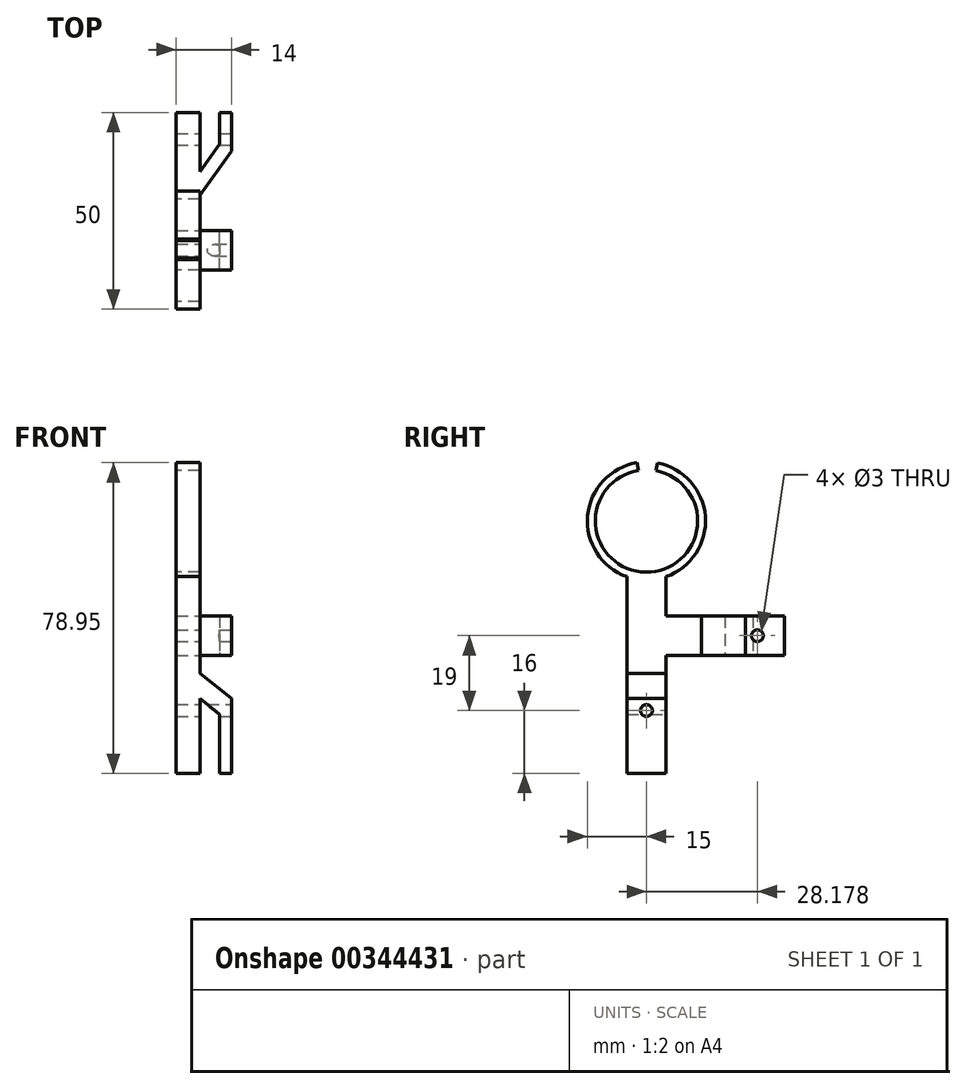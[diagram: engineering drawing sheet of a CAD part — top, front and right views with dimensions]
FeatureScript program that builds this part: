
annotation { "Feature Type Name" : "Feature", "Feature Type Description" : "" }
export const myFeature = defineFeature(function(context is Context, id is Id, definition is map)
    precondition{}
    {
        {
            var Q0;
            Q0=qCreatedBy(makeId("Front.planeOp"),FACE);
            var sketch = newSketch(context, id + "F0", { "sketchPlane" : qUnion([Q0])});
            skLineSegment(sketch, "E0", {"start": v(0, 0) * mm, "end": v(0, 50) * mm});
            skLineSegment(sketch, "E1", {"start": v(6, 50) * mm, "end": v(6, 25.4) * mm});
            skLineSegment(sketch, "E2", {"start": v(6, 25.4) * mm, "end": v(14, 19) * mm});
            skLineSegment(sketch, "E3", {"start": v(14, 19) * mm, "end": v(14, 0) * mm});
            skLineSegment(sketch, "E4", {"start": v(14, 0) * mm, "end": v(11, 0) * mm});
            skLineSegment(sketch, "E5", {"start": v(11, 0) * mm, "end": v(11, 15) * mm});
            skLineSegment(sketch, "E6", {"start": v(11, 15) * mm, "end": v(6, 19) * mm});
            skLineSegment(sketch, "E7", {"start": v(6, 19) * mm, "end": v(6, 0) * mm});
            skLineSegment(sketch, "E8", {"start": v(6, 0) * mm, "end": v(0, 0) * mm});
            skLineSegment(sketch, "E9", {"start": v(6, 50) * mm, "end": v(0, 50) * mm});
            skSolve(sketch);
        }
        {
            var Q0;
            Q0 = qSketchRegion(id + "F0", true);
            extrude(context, id + "F1", {"entities" : qUnion([Q0]), "depth" : 10 * mm});
        }
        {
            var Q0;
            Q0=makeQuery(id+"F1.opExtrude","SWEPT_FACE",FACE,{"disambiguationData":[OSD([sQuery(id+"F0.wireOp",EDGE,"E3")])]});
            var sketch = newSketch(context, id + "F2", { "sketchPlane" : qUnion([Q0])});
            skCircle(sketch, "E10", {"center": v(-5, 16) * mm, "radius": 1.5 * mm});
            skPoint(sketch, "E10.centerSnap0", {"position": v(-5, 19) * mm});
            skSolve(sketch);
        }
        {
            var Q0;
            Q0 = qSketchRegion(id + "F2", true);
            extrude(context, id + "F3", {"entities" : qUnion([Q0]), "operationType" : NewBodyOperationType.REMOVE, "oppositeDirection" : true, "depth" : 25 * mm});
        }
        {
            var Q0;
            Q0=qCreatedBy(makeId("Top.planeOp"),FACE);
            cPlane(context, id + "F4", {"entities" : qUnion([Q0]), "cplaneType" : CPlaneType.OFFSET, "offset" : 30 * mm, "width" : 150 * mm, "height" : 150 * mm});
        }
        {
            var Q0;
            Q0=qCreatedBy(id+"F4.planeOp",FACE);
            var sketch = newSketch(context, id + "F5", { "sketchPlane" : qUnion([Q0])});
            skLineSegment(sketch, "E11", {"start": v(6, 0) * mm, "end": v(6, 8.98) * mm});
            skLineSegment(sketch, "E12", {"start": v(14, 30) * mm, "end": v(11, 30) * mm});
            skLineSegment(sketch, "E13", {"start": v(11, 30) * mm, "end": v(11, 22) * mm});
            skLineSegment(sketch, "E14", {"start": v(6, 15) * mm, "end": v(6, 30) * mm});
            skLineSegment(sketch, "E15", {"start": v(6, 30) * mm, "end": v(0, 30) * mm});
            skLineSegment(sketch, "E16", {"start": v(0, 30) * mm, "end": v(0, 0) * mm});
            skLineSegment(sketch, "E17", {"start": v(0, 0) * mm, "end": v(6, 0) * mm});
            skLineSegment(sketch, "E18", {"start": v(14, 30) * mm, "end": v(14, 20.18) * mm});
            skLineSegment(sketch, "E19", {"start": v(14, 20.18) * mm, "end": v(6, 8.98) * mm});
            skLineSegment(sketch, "E20", {"start": v(11, 22) * mm, "end": v(6, 15) * mm});
            skSolve(sketch);
        }
        {
            var Q0;
            Q0 = qSketchRegion(id + "F5", true);
            extrude(context, id + "F6", {"entities" : qUnion([Q0]), "operationType" : NewBodyOperationType.ADD, "depth" : 10 * mm});
        }
        {
            var Q0;
            Q0=makeQuery(id+"F6.opExtrude","SWEPT_FACE",FACE,{"disambiguationData":[OSD([sQuery(id+"F5.wireOp",EDGE,"E18")])]});
            var sketch = newSketch(context, id + "F7", { "sketchPlane" : qUnion([Q0])});
            skCircle(sketch, "E21", {"center": v(23.18, 35) * mm, "radius": 1.5 * mm});
            skSolve(sketch);
        }
        {
            var Q0;
            Q0 = qSketchRegion(id + "F7", true);
            extrude(context, id + "F8", {"entities" : qUnion([Q0]), "operationType" : NewBodyOperationType.REMOVE, "oppositeDirection" : true, "depth" : 25 * mm});
        }
        {
            var Q0;
            Q0=qCreatedBy(makeId("Right.planeOp"),FACE);
            var sketch = newSketch(context, id + "F9", { "sketchPlane" : qUnion([Q0])});
            skArc(sketch, "E22", {"start": v(-7.38, 78.95) * mm, "mid": v(-5.22, 49.14) * mm, "end": v(-2.17, 78.87) * mm});
            skArc(sketch, "E23", {"start": v(-7.07, 76.98) * mm, "mid": v(-5.2, 51.14) * mm, "end": v(-2.55, 76.9) * mm});
            skLineSegment(sketch, "E24", {"start": v(-7.07, 76.98) * mm, "end": v(-7.38, 78.95) * mm});
            skLineSegment(sketch, "E25", {"start": v(-2.17, 78.87) * mm, "end": v(-2.55, 76.9) * mm});
            skSolve(sketch);
        }
        {
            var Q0;
            Q0 = qSketchRegion(id + "F9", true);
            extrude(context, id + "F10", {"entities" : qUnion([Q0]), "operationType" : NewBodyOperationType.ADD, "depth" : 6 * mm});
        }
    });
